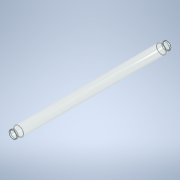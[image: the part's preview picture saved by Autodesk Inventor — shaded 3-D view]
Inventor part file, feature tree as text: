
AUTODESK INVENTOR PART (.ipt)
format: ipt  version: 2020 (Build 240168000, 168)  size: 135,680 bytes
history: native  units: mm
features: sketch x2, extrude x1, revolve x1, fillet x1, mirror x1
ambient origin geometry x8: Origin, YZ Plane, XZ Plane, XY Plane, X Axis, Y Axis, Z Axis, Center Point
bodies: Solid1 (feature_tree)
feature tree (6):
  extrude  "Extrusion1"  Depth=2.0mm
  revolve  "Revolution1"  [1 undecoded]
  fillet  "Fillet2"  Radius=2.0mm
  mirror  "Mirror1"
  sketch  "Sketch1"  dims[d0=30.0mm d1=2.0mm]
  sketch  "Sketch2"  dims[d2=480.0mm d3=0.0mm d4=2.0mm d5=2.0mm d8=12.0mm d10=5.0mm d11=90.0deg d13=20.0mm d14=1.0mm]
note: 1 required parameter value undecoded (feature->parameter linkage not recoverable at this tier; creation-order binding heuristic only, values carry confidence <= 0.55)
